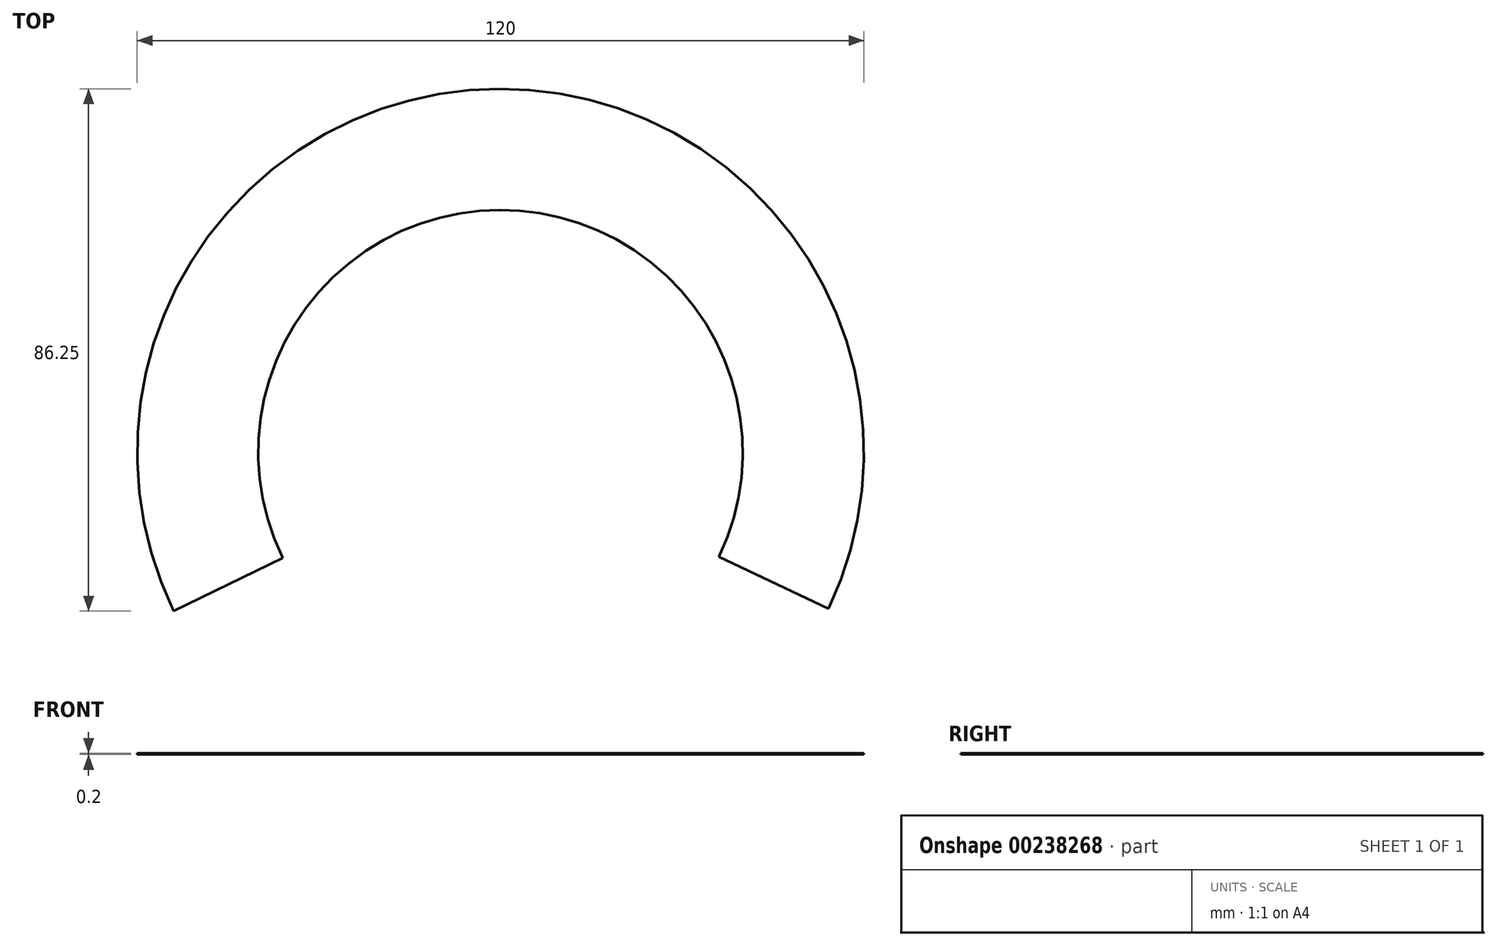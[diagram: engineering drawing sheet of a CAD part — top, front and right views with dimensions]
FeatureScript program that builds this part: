
annotation { "Feature Type Name" : "Feature", "Feature Type Description" : "" }
export const myFeature = defineFeature(function(context is Context, id is Id, definition is map)
    precondition{}
    {
        {
            var Q0;
            Q0=qCreatedBy(makeId("Top.planeOp"),FACE);
            var sketch = newSketch(context, id + "F0", { "sketchPlane" : qUnion([Q0])});
            skArc(sketch, "E0", {"start": v(36.08, -17.26) * mm, "mid": v(-0.13, 40) * mm, "end": v(-35.97, -17.5) * mm});
            skArc(sketch, "E1", {"start": v(54.13, -25.89) * mm, "mid": v(-0.2, 60) * mm, "end": v(-53.95, -26.25) * mm});
            skLineSegment(sketch, "E2", {"start": v(36.08, -17.26) * mm, "end": v(54.13, -25.89) * mm});
            skLineSegment(sketch, "E3", {"start": v(54.13, -25.89) * mm, "end": v(36.08, -17.26) * mm});
            skLineSegment(sketch, "E4", {"start": v(-35.97, -17.5) * mm, "end": v(-53.95, -26.25) * mm});
            skSolve(sketch);
        }
        {
            var Q0;
            Q0=makeQuery(id+"F0.imprint","IMPRINT",FACE,{"disambiguationData":[TD([[makeQuery(id+"F0.imprint","IMPRINT",EDGE,{"derivedFrom":sQuery(id+"F0.wireOp",EDGE,"E0")}),-1.0]])]});
            extrude(context, id + "F1", {"entities" : qUnion([Q0]), "depth" : 0.2 * mm});
        }
    });
